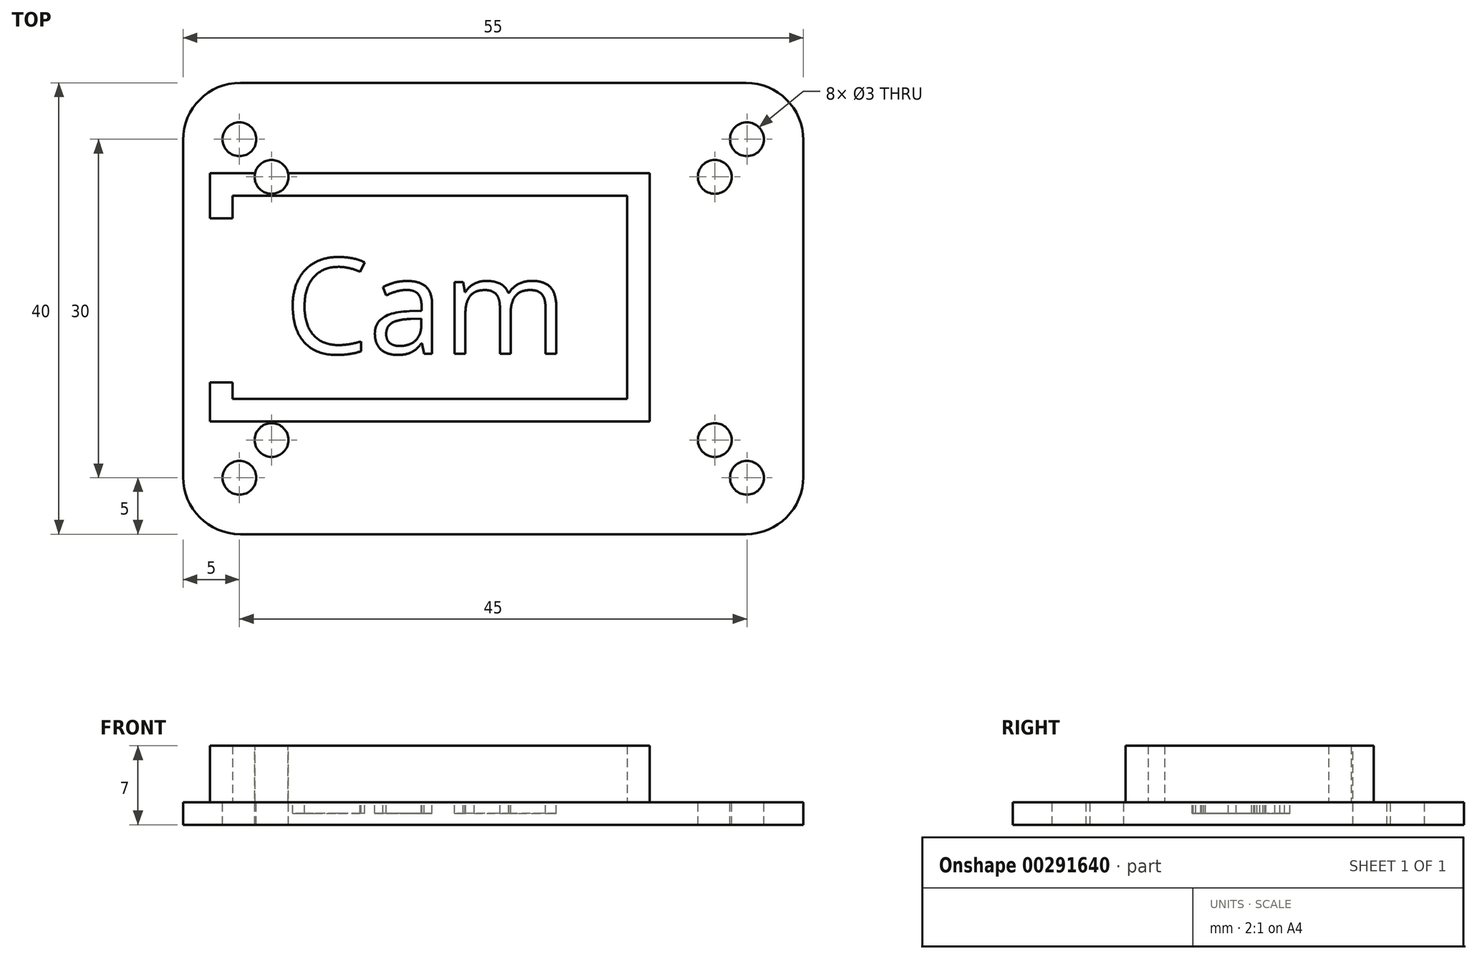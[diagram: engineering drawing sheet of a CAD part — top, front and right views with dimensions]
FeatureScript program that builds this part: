
annotation { "Feature Type Name" : "Feature", "Feature Type Description" : "" }
export const myFeature = defineFeature(function(context is Context, id is Id, definition is map)
    precondition{}
    {
        {
            var Q0;
            Q0=qCreatedBy(makeId("Top.planeOp"),FACE);
            var sketch = newSketch(context, id + "F0", { "sketchPlane" : qUnion([Q0])});
            skLineSegment(sketch, "E0.bottom", {"start": v(0, 0) * mm, "end": v(55, 0) * mm});
            skLineSegment(sketch, "E0.top", {"start": v(0, 40) * mm, "end": v(55, 40) * mm});
            skLineSegment(sketch, "E0.left", {"start": v(0, 0) * mm, "end": v(0, 40) * mm});
            skLineSegment(sketch, "E0.right", {"start": v(55, 0) * mm, "end": v(55, 40) * mm});
            skSolve(sketch);
        }
        {
            var Q0;
            Q0=qSketchRegion(id+"F0",true);
            extrude(context, id + "F1", {"entities" : qUnion([Q0]), "depth" : 2 * mm, "offsetDistance" : 25.4 * mm});
        }
        {
            var Q0;
            Q0=makeQuery(id+"F1.opExtrude","CAP_FACE",FACE,{"disambiguationData":[OSD([sQuery(id+"F0.wireOp",EDGE,"E0.bottom"),sQuery(id+"F0.wireOp",EDGE,"E0.top"),sQuery(id+"F0.wireOp",EDGE,"E0.left"),sQuery(id+"F0.wireOp",EDGE,"E0.right")])],"isStart":false});
            cPlane(context, id + "F2", {"entities" : qUnion([Q0]), "cplaneType" : CPlaneType.OFFSET, "offset" : 0 * mm, "width" : 152.4 * mm, "height" : 152.4 * mm});
        }
        {
            var Q0;
            Q0=makeQuery(id+"F1.opExtrude","SWEPT_EDGE",EDGE,{"disambiguationData":[OSD([sQuery(id+"F0.wireOp",EDGE,"E0.bottom"),sQuery(id+"F0.wireOp",EDGE,"E0.right")])]});
            fillet(context, id + "F3", {"entities" : qUnion([Q0]), "radius" : 5.08 * mm, "tangentPropagation" : true, "allowEdgeOverflow" : false});
        }
        {
            var Q0;
            Q0=makeQuery(id+"F1.opExtrude","SWEPT_EDGE",EDGE,{"disambiguationData":[OSD([sQuery(id+"F0.wireOp",EDGE,"E0.top"),sQuery(id+"F0.wireOp",EDGE,"E0.right")])]});
            fillet(context, id + "F4", {"entities" : qUnion([Q0]), "radius" : 5.08 * mm, "tangentPropagation" : true, "allowEdgeOverflow" : false});
        }
        {
            var Q0;
            Q0=makeQuery(id+"F1.opExtrude","SWEPT_EDGE",EDGE,{"disambiguationData":[OSD([sQuery(id+"F0.wireOp",EDGE,"E0.top"),sQuery(id+"F0.wireOp",EDGE,"E0.left")])]});
            fillet(context, id + "F5", {"entities" : qUnion([Q0]), "radius" : 5.08 * mm, "tangentPropagation" : true, "allowEdgeOverflow" : false});
        }
        {
            var Q0;
            Q0=makeQuery(id+"F1.opExtrude","SWEPT_EDGE",EDGE,{"disambiguationData":[OSD([sQuery(id+"F0.wireOp",EDGE,"E0.bottom"),sQuery(id+"F0.wireOp",EDGE,"E0.left")])]});
            fillet(context, id + "F6", {"entities" : qUnion([Q0]), "radius" : 5.08 * mm, "tangentPropagation" : true, "allowEdgeOverflow" : false});
        }
        {
            var Q0;
            Q0=qCreatedBy(id+"F2.planeOp",FACE);
            var sketch = newSketch(context, id + "F7", { "sketchPlane" : qUnion([Q0])});
            skLineSegment(sketch, "E1", {"start": v(27.5, 0) * mm, "end": v(27.5, 70.78) * mm});
            skLineSegment(sketch, "E2", {"start": v(0, 20) * mm, "end": v(105.16, 20) * mm});
            skSolve(sketch);
        }
        {
            var Q0;
            Q0=qCreatedBy(id+"F2.planeOp",FACE);
            var sketch = newSketch(context, id + "F8", { "sketchPlane" : qUnion([Q0])});
            skLineSegment(sketch, "E3.bottom", {"start": v(4, 30) * mm, "end": v(39, 30) * mm});
            skLineSegment(sketch, "E3.top", {"start": v(4, 12) * mm, "end": v(39, 12) * mm});
            skLineSegment(sketch, "E3.right", {"start": v(39, 30) * mm, "end": v(39, 12) * mm});
            skText(sketch, "E4", { "text": "Cam", "fontName": "OpenSans-Regular.ttf"});
            skLineSegment(sketch, "E5", {"start": v(4, 28) * mm, "end": v(2, 28) * mm});
            skLineSegment(sketch, "E6", {"start": v(2, 28) * mm, "end": v(2, 32) * mm});
            skLineSegment(sketch, "E7", {"start": v(2, 32) * mm, "end": v(41, 32) * mm});
            skLineSegment(sketch, "E8", {"start": v(41, 32) * mm, "end": v(41, 10) * mm});
            skLineSegment(sketch, "E9", {"start": v(41, 10) * mm, "end": v(2, 10) * mm});
            skLineSegment(sketch, "E10", {"start": v(2, 10) * mm, "end": v(2, 13.44) * mm});
            skLineSegment(sketch, "E11", {"start": v(2, 13.44) * mm, "end": v(4, 13.44) * mm});
            skLineSegment(sketch, "E12", {"start": v(4, 13.44) * mm, "end": v(4, 12) * mm});
            skLineSegment(sketch, "E13", {"start": v(4, 28) * mm, "end": v(4, 30) * mm});
            const initialGuessF8  = {"E4": [0.009, 0.016, 1, 0, 0.00852]};
            skSetInitialGuess(sketch, initialGuessF8);
            skSolve(sketch);
        }
        {
            var Q0;
            Q0=makeQuery(id+"F8.imprint","IMPRINT",FACE,{"disambiguationData":[TD([[makeQuery(id+"F8.imprint","IMPRINT",EDGE,{"derivedFrom":sQuery(id+"F8.wireOp",EDGE,"E4.sketch_text.stroke-0")}),-1.0]])]});
            var Q1;
            Q1=makeQuery(id+"F8.imprint","IMPRINT",FACE,{"disambiguationData":[TD([[makeQuery(id+"F8.imprint","IMPRINT",EDGE,{"derivedFrom":sQuery(id+"F8.wireOp",EDGE,"E4.sketch_text.stroke-15")}),-1.0]])]});
            var Q2;
            Q2=makeQuery(id+"F8.imprint","IMPRINT",FACE,{"disambiguationData":[TD([[makeQuery(id+"F8.imprint","IMPRINT",EDGE,{"derivedFrom":sQuery(id+"F8.wireOp",EDGE,"E4.sketch_text.stroke-42")}),-1.0]])]});
            extrude(context, id + "F9", {"entities" : qUnion([Q0, Q1, Q2]), "operationType" : NewBodyOperationType.REMOVE, "oppositeDirection" : true, "depth" : 1 * mm, "offsetDistance" : 25.4 * mm});
        }
        {
            var Q0;
            Q0=qCreatedBy(id+"F2.planeOp",FACE);
            var sketch = newSketch(context, id + "F10", { "sketchPlane" : qUnion([Q0])});
            skLineSegment(sketch, "E14.bottom", {"start": v(4.38, 30) * mm, "end": v(39.38, 30) * mm});
            skLineSegment(sketch, "E14.top", {"start": v(4.38, 12) * mm, "end": v(39.38, 12) * mm});
            skLineSegment(sketch, "E14.right", {"start": v(39.38, 30) * mm, "end": v(39.38, 12) * mm});
            skLineSegment(sketch, "E15", {"start": v(4.38, 28) * mm, "end": v(2.38, 28) * mm});
            skLineSegment(sketch, "E16", {"start": v(2.38, 28) * mm, "end": v(2.38, 32) * mm});
            skLineSegment(sketch, "E17", {"start": v(2.38, 32) * mm, "end": v(41.38, 32) * mm});
            skLineSegment(sketch, "E18", {"start": v(41.38, 32) * mm, "end": v(41.38, 10) * mm});
            skLineSegment(sketch, "E19", {"start": v(41.38, 10) * mm, "end": v(2.38, 10) * mm});
            skLineSegment(sketch, "E20", {"start": v(2.38, 10) * mm, "end": v(2.38, 13.44) * mm});
            skLineSegment(sketch, "E21", {"start": v(2.38, 13.44) * mm, "end": v(4.38, 13.44) * mm});
            skLineSegment(sketch, "E22", {"start": v(4.38, 13.44) * mm, "end": v(4.38, 12) * mm});
            skLineSegment(sketch, "E23", {"start": v(4.38, 28) * mm, "end": v(4.38, 30) * mm});
            skSolve(sketch);
        }
        {
            var Q0;
            Q0=qSketchRegion(id+"F10",true);
            extrude(context, id + "F11", {"entities" : qUnion([Q0]), "operationType" : NewBodyOperationType.ADD, "depth" : 5 * mm, "offsetDistance" : 25.4 * mm});
        }
        {
            var Q0;
            Q0=qCreatedBy(id+"F2.planeOp",FACE);
            var sketch = newSketch(context, id + "F12", { "sketchPlane" : qUnion([Q0])});
            skCircle(sketch, "E24", {"center": v(50, 5) * mm, "radius": 1.5 * mm});
            skCircle(sketch, "E25", {"center": v(47.15, 8.34) * mm, "radius": 1.5 * mm});
            skCircle(sketch, "E26.MirrorC", {"center": v(47.15, 31.66) * mm, "radius": 1.5 * mm});
            skCircle(sketch, "E27.MirrorC", {"center": v(50, 35) * mm, "radius": 1.5 * mm});
            skCircle(sketch, "E28.MirrorC", {"center": v(7.85, 31.66) * mm, "radius": 1.5 * mm});
            skCircle(sketch, "E29.MirrorC", {"center": v(5, 35) * mm, "radius": 1.5 * mm});
            skCircle(sketch, "E30.MirrorC", {"center": v(7.85, 8.34) * mm, "radius": 1.5 * mm});
            skCircle(sketch, "E31.MirrorC", {"center": v(5, 5) * mm, "radius": 1.5 * mm});
            skSolve(sketch);
        }
        {
            var Q0;
            Q0=qSketchRegion(id+"F12",true);
            extrude(context, id + "F13", {"entities" : qUnion([Q0]), "operationType" : NewBodyOperationType.REMOVE, "endBound" : BoundingType.SYMMETRIC, "oppositeDirection" : true, "depth" : 25.4 * mm, "offsetDistance" : 25.4 * mm});
        }
    });
